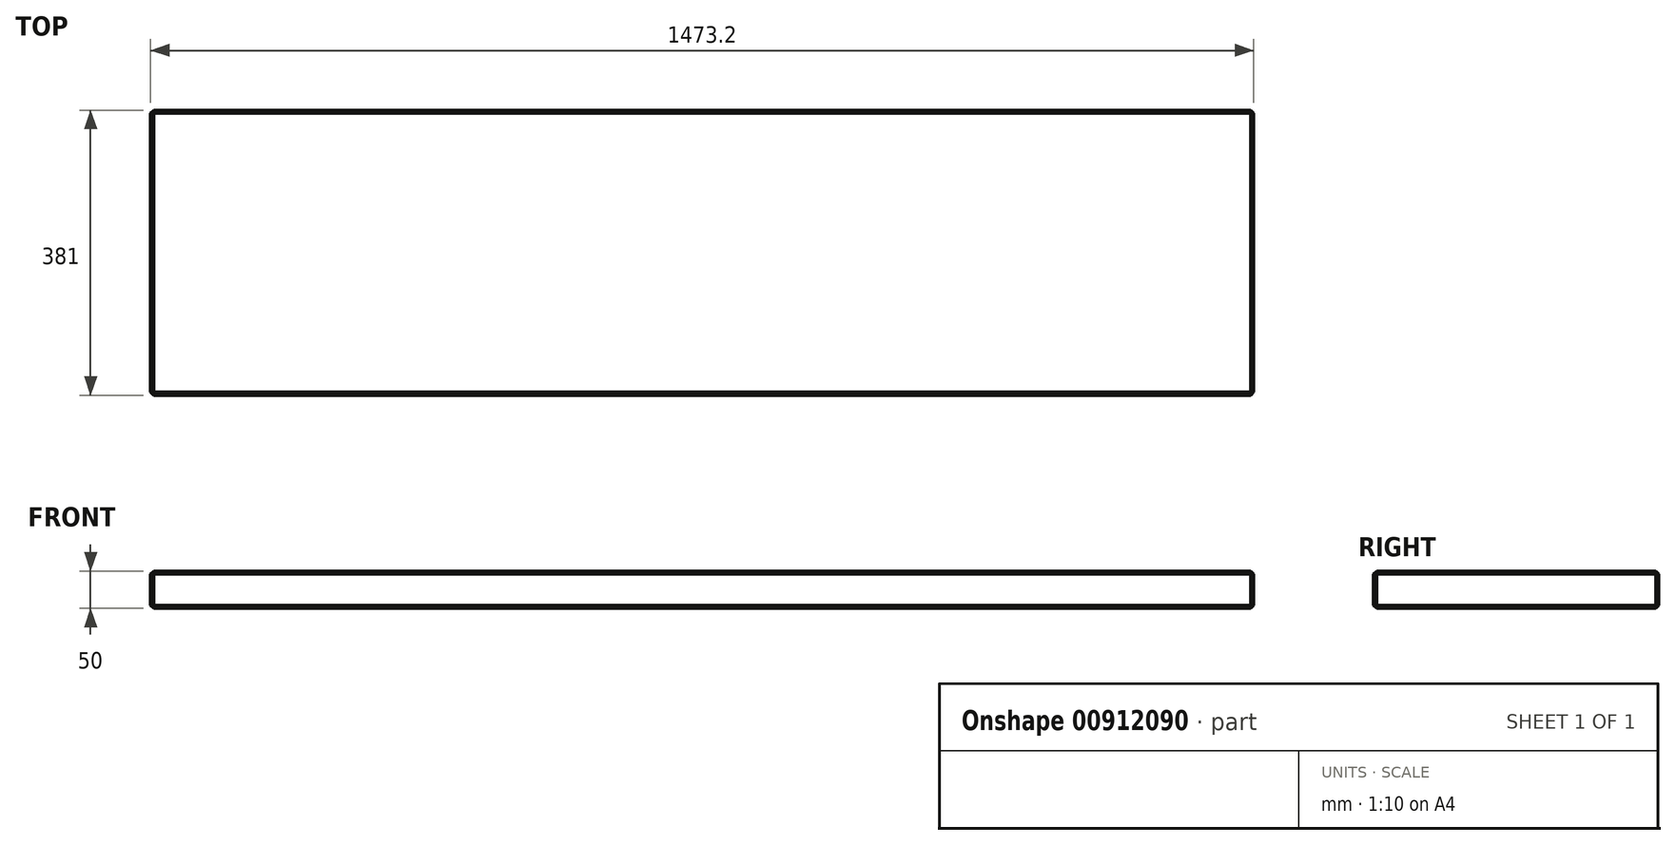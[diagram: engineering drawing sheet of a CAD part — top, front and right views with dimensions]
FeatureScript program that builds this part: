
annotation { "Feature Type Name" : "Feature", "Feature Type Description" : "" }
export const myFeature = defineFeature(function(context is Context, id is Id, definition is map)
    precondition{}
    {
        {
            var Q0;
            Q0=qCreatedBy(makeId("Top.planeOp"),FACE);
            var sketch = newSketch(context, id + "F0", { "sketchPlane" : qUnion([Q0])});
            skLineSegment(sketch, "E0.bottom", {"start": v(1473.2, 381) * mm, "end": v(0, 381) * mm});
            skLineSegment(sketch, "E0.top", {"start": v(1473.2, 0) * mm, "end": v(0, 0) * mm});
            skLineSegment(sketch, "E0.left", {"start": v(1473.2, 381) * mm, "end": v(1473.2, 0) * mm});
            skLineSegment(sketch, "E0.right", {"start": v(0, 381) * mm, "end": v(0, 0) * mm});
            skSolve(sketch);
        }
        {
            var Q0;
            Q0=makeQuery(id+"F0.imprint","IMPRINT",FACE,{"disambiguationData":[TD([[makeQuery(id+"F0.imprint","IMPRINT",EDGE,{"derivedFrom":sQuery(id+"F0.wireOp",EDGE,"E0.bottom")}),1.0]])]});
            extrude(context, id + "F1", {"entities" : qUnion([Q0]), "depth" : 50 * mm, "offsetDistance" : 25.4 * mm});
        }
        {
            var Q0;
            Q0=makeQuery(id+"F1.opExtrude","CAP_EDGE",EDGE,{"disambiguationData":[OSD([sQuery(id+"F0.wireOp",EDGE,"E0.left")])],"isStart":false});
            var Q1;
            Q1=makeQuery(id+"F1.opExtrude","CAP_EDGE",EDGE,{"disambiguationData":[OSD([sQuery(id+"F0.wireOp",EDGE,"E0.bottom")])],"isStart":false});
            var Q2;
            Q2=makeQuery(id+"F1.opExtrude","CAP_EDGE",EDGE,{"disambiguationData":[OSD([sQuery(id+"F0.wireOp",EDGE,"E0.left")])],"isStart":true});
            var Q3;
            Q3=makeQuery(id+"F1.opExtrude","SWEPT_FACE",FACE,{"disambiguationData":[OSD([sQuery(id+"F0.wireOp",EDGE,"E0.left")])]});
            var Q4;
            Q4=makeQuery(id+"F1.opExtrude","CAP_EDGE",EDGE,{"disambiguationData":[OSD([sQuery(id+"F0.wireOp",EDGE,"E0.top")])],"isStart":false});
            var Q5;
            Q5=makeQuery(id+"F1.opExtrude","CAP_EDGE",EDGE,{"disambiguationData":[OSD([sQuery(id+"F0.wireOp",EDGE,"E0.top")])],"isStart":true});
            var Q6;
            Q6=makeQuery(id+"F1.opExtrude","SWEPT_EDGE",EDGE,{"disambiguationData":[OSD([sQuery(id+"F0.wireOp",EDGE,"E0.top"),sQuery(id+"F0.wireOp",EDGE,"E0.left")])]});
            var Q7;
            Q7=makeQuery(id+"F1.opExtrude","CAP_EDGE",EDGE,{"disambiguationData":[OSD([sQuery(id+"F0.wireOp",EDGE,"E0.bottom")])],"isStart":true});
            var Q8;
            Q8=makeQuery(id+"F1.opExtrude","CAP_EDGE",EDGE,{"disambiguationData":[OSD([sQuery(id+"F0.wireOp",EDGE,"E0.right")])],"isStart":true});
            var Q9;
            Q9=makeQuery(id+"F1.opExtrude","SWEPT_EDGE",EDGE,{"disambiguationData":[OSD([sQuery(id+"F0.wireOp",EDGE,"E0.bottom"),sQuery(id+"F0.wireOp",EDGE,"E0.right")])]});
            var Q10;
            Q10=makeQuery(id+"F1.opExtrude","CAP_EDGE",EDGE,{"disambiguationData":[OSD([sQuery(id+"F0.wireOp",EDGE,"E0.right")])],"isStart":false});
            var Q11;
            Q11=makeQuery(id+"F1.opExtrude","SWEPT_EDGE",EDGE,{"disambiguationData":[OSD([sQuery(id+"F0.wireOp",EDGE,"E0.top"),sQuery(id+"F0.wireOp",EDGE,"E0.right")])]});
            var Q12;
            Q12=makeQuery(id+"F1.opExtrude","SWEPT_EDGE",EDGE,{"disambiguationData":[OSD([sQuery(id+"F0.wireOp",EDGE,"E0.bottom"),sQuery(id+"F0.wireOp",EDGE,"E0.left")])]});
            chamfer(context, id + "F2", {"entities" : qUnion([Q0, Q1, Q2, Q3, Q4, Q5, Q6, Q7, Q8, Q9, Q10, Q11, Q12]), "width" : 4 * mm, "tangentPropagation" : true});
        }
    });
